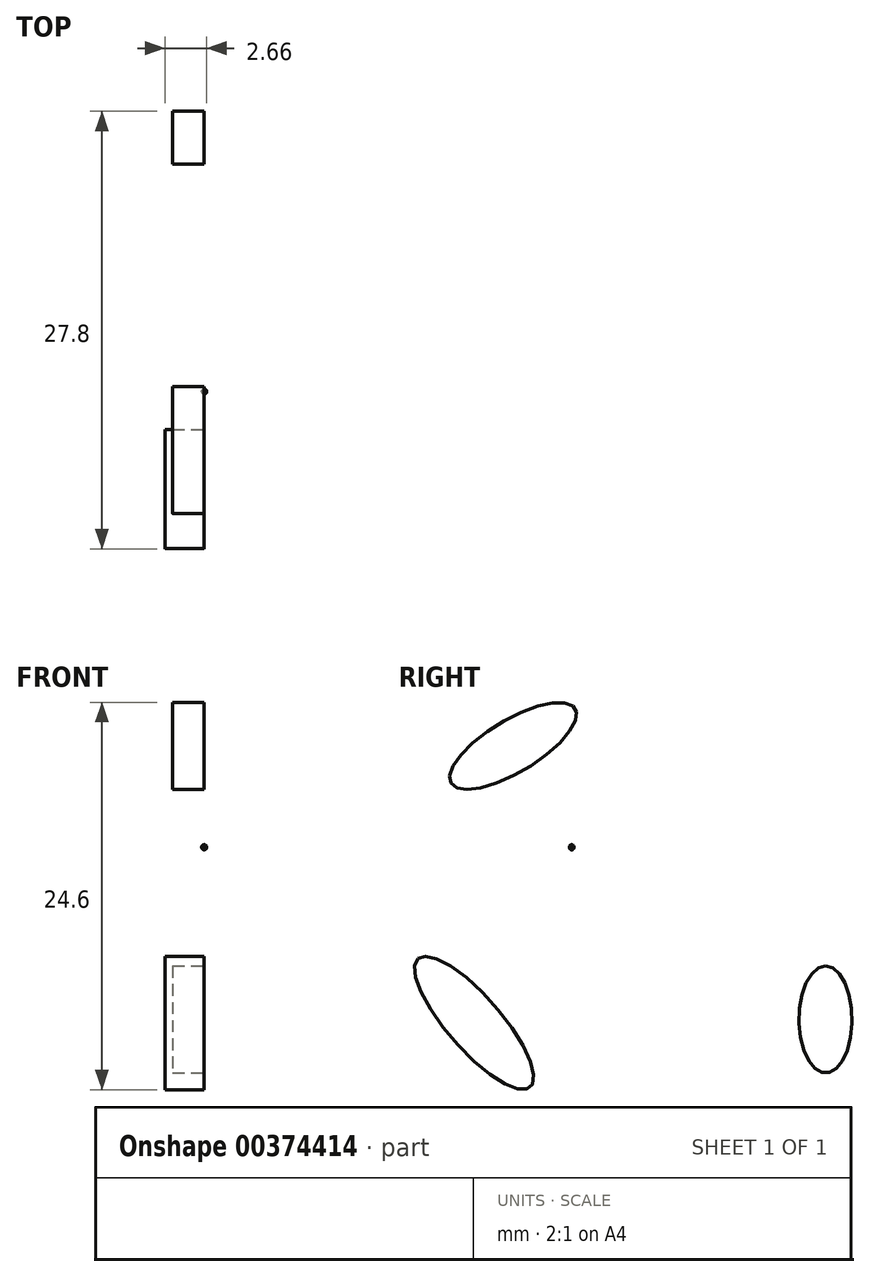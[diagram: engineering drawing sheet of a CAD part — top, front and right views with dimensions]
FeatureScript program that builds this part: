
annotation { "Feature Type Name" : "Feature", "Feature Type Description" : "" }
export const myFeature = defineFeature(function(context is Context, id is Id, definition is map)
    precondition{}
    {
        {
            var Q0;
            Q0=qCreatedBy(makeId("Front.planeOp"),FACE);
            var sketch = newSketch(context, id + "F0", { "sketchPlane" : qUnion([Q0])});
            skLineSegment(sketch, "E0", {"start": v(0, 0) * mm, "end": v(0, 20) * mm});
            skLineSegment(sketch, "E1", {"start": v(0, 0) * mm, "end": v(20.9, 0) * mm});
            skArc(sketch, "E2", {"start": v(20.9, 0) * mm, "mid": v(14.71, 14.46) * mm, "end": v(0, 20) * mm});
            skSolve(sketch);
        }
        {
            var Q0;
            Q0=makeQuery(id+"F0.imprint","IMPRINT",FACE,{"disambiguationData":[TD([[makeQuery(id+"F0.imprint","IMPRINT",EDGE,{"derivedFrom":sQuery(id+"F0.wireOp",EDGE,"E0")}),-1.0]])]});
            var Q1;
            Q1=sQuery(id+"F0.wireOp",EDGE,"E1");
            revolve(context, id + "F1", {"entities" : qUnion([Q0]), "axis" : qUnion([Q1]), "revolveType" : RevolveType.FULL});
        }
        {
            var Q0;
            Q0=qCreatedBy(makeId("Right.planeOp"),FACE);
            var sketch = newSketch(context, id + "F2", { "sketchPlane" : qUnion([Q0])});
            skLineSegment(sketch, "E3", {"start": v(0, 0) * mm, "end": v(0, 3) * mm});
            skLineSegment(sketch, "E4", {"start": v(0, 0) * mm, "end": v(-3, 0) * mm});
            skArc(sketch, "E5", {"start": v(0, 3) * mm, "mid": v(-2.14, 2.14) * mm, "end": v(-3, 0) * mm});
            skSolve(sketch);
        }
        {
            var Q0;
            Q0=qSketchRegion(id+"F2",true);
            var Q1;
            Q1=sQuery(id+"F2.wireOp",EDGE,"E4");
            revolve(context, id + "F3", {"operationType" : NewBodyOperationType.ADD, "entities" : qUnion([Q0]), "axis" : qUnion([Q1]), "revolveType" : RevolveType.FULL});
        }
        {
            var Q0;
            Q0=makeQuery(id+"F1.opRevolve","SWEPT_FACE",FACE,{"disambiguationData":[OSD([sQuery(id+"F0.wireOp",EDGE,"E0")])]});
            var sketch = newSketch(context, id + "F4", { "sketchPlane" : qUnion([Q0])});
            skLineSegment(sketch, "E6", {"start": v(0, 0) * mm, "end": v(-3, 0) * mm});
            skLineSegment(sketch, "E7", {"start": v(0, 0) * mm, "end": v(0, 3) * mm});
            skArc(sketch, "E8", {"start": v(0, 3) * mm, "mid": v(-2.1, 2.1) * mm, "end": v(-3, 0) * mm});
            skSolve(sketch);
        }
        {
            var Q0;
            Q0=makeQuery(id+"F4.imprint","IMPRINT",FACE,{"disambiguationData":[TD([[makeQuery(id+"F4.imprint","IMPRINT",EDGE,{"derivedFrom":sQuery(id+"F4.wireOp",EDGE,"E6")}),-1.0]])]});
            var Q1;
            Q1=sQuery(id+"F4.wireOp",EDGE,"E6");
            revolve(context, id + "F5", {"operationType" : NewBodyOperationType.ADD, "entities" : qUnion([Q0]), "axis" : qUnion([Q1]), "revolveType" : RevolveType.FULL});
        }
        {
            var Q0;
            Q0=makeQuery(id+"F1.opRevolve","SWEPT_FACE",FACE,{"disambiguationData":[OSD([sQuery(id+"F0.wireOp",EDGE,"E0")])]});
            var sketch = newSketch(context, id + "F6", { "sketchPlane" : qUnion([Q0])});
            skEllipse(sketch, "E9", {"center": v(9.46, -7.67) * mm, "majorRadius": 5.42 * mm, "minorRadius": 1.7 * mm, "majorAxis": v(0.66, 0.75)});
            skSolve(sketch);
        }
        {
            var Q0;
            Q0=qSketchRegion(id+"F6",true);
            extrude(context, id + "F7", {"entities" : qUnion([Q0]), "depth" : 2.5 * mm});
        }
        {
            var Q0;
            Q0=makeQuery(id+"F7.opExtrude","CAP_FACE",FACE,{"disambiguationData":[OSD([sQuery(id+"F6.wireOp",EDGE,"E9")])],"isStart":false});
            var sketch = newSketch(context, id + "F8", { "sketchPlane" : qUnion([Q0])});
            skFitSpline(sketch, "E10", {"points": [v(7.97, -11.28) * mm, v(6.8, -8.9) * mm, v(9.38, -10.19) * mm, v(8.17, -7.24) * mm, v(11, -8.49) * mm, v(9.27, -5.4) * mm, v(11.92, -6.7) * mm, v(11.05, -4) * mm, v(13.1, -5.01) * mm], "startDerivative": vector(-20.7, 30.85) * mm, "endDerivative": vector(27.66, -19.9) * mm});
            skSolve(sketch);
        }
        {
            var Q0;
            Q0=qSketchRegion(id+"F8",true);
            var Q1;
            Q1=sQuery(id+"F8.wireOp",EDGE,"E10");
            extrude(context, id + "F9", {"entities" : qUnion([Q0]), "bodyType" : ToolBodyType.SURFACE, "surfaceEntities" : qUnion([Q1]), "oppositeDirection" : true, "depth" : 2 * mm});
        }
        {
            var Q0;
            Q0=makeQuery(id+"F1.opRevolve","SWEPT_FACE",FACE,{"disambiguationData":[OSD([sQuery(id+"F0.wireOp",EDGE,"E0")])]});
            var sketch = newSketch(context, id + "F10", { "sketchPlane" : qUnion([Q0])});
            skSolve(sketch);
        }
        {
            var Q0;
            {var subQ1=sQuery(id+"F0.wireOp",EDGE,"E0");Q0=makeQuery(id+"F10.imprint","IMPRINT",FACE,{"disambiguationData":[TD([[makeQuery(id+"F10.imprint","IMPRINT",EDGE,{"derivedFrom":makeQuery(id+"F1.opRevolve","SWEPT_EDGE",EDGE,{"disambiguationData":[OSD([subQ1,sQuery(id+"F0.wireOp",EDGE,"E2")])]})}),1.0]])]});}
            var sketch = newSketch(context, id + "F11", { "sketchPlane" : qUnion([Q0])});
            skSolve(sketch);
        }
        {
            var Q0;
            {var subQ1=sQuery(id+"F0.wireOp",EDGE,"E0");Q0=makeQuery(id+"F10.imprint","IMPRINT",FACE,{"disambiguationData":[TD([[makeQuery(id+"F10.imprint","IMPRINT",EDGE,{"derivedFrom":makeQuery(id+"F1.opRevolve","SWEPT_EDGE",EDGE,{"disambiguationData":[OSD([subQ1,sQuery(id+"F0.wireOp",EDGE,"E2")])]})}),1.0]])]});}
            var sketch = newSketch(context, id + "F12", { "sketchPlane" : qUnion([Q0])});
            skEllipse(sketch, "E11", {"center": v(6.98, 9.93) * mm, "majorRadius": 4.6 * mm, "minorRadius": 1.66 * mm, "majorAxis": v(0.86, -0.51)});
            skSolve(sketch);
        }
        {
            var Q0;
            Q0=qSketchRegion(id+"F12",true);
            extrude(context, id + "F13", {"entities" : qUnion([Q0]), "depth" : 2 * mm});
        }
        {
            var Q0;
            Q0=makeQuery(id+"F13.opExtrude","CAP_FACE",FACE,{"disambiguationData":[OSD([sQuery(id+"F12.wireOp",EDGE,"E11")])],"isStart":false});
            var sketch = newSketch(context, id + "F14", { "sketchPlane" : qUnion([Q0])});
            skFitSpline(sketch, "E12", {"points": [v(4.68, 12.63) * mm, v(3.63, 10.54) * mm, v(6.2, 12.18) * mm, v(5.11, 9.18) * mm, v(7.84, 11.35) * mm, v(6.92, 8.06) * mm, v(9.45, 10.2) * mm, v(9.08, 7.26) * mm], "startDerivative": vector(-17.32, -26.87) * mm, "endDerivative": vector(-10.03, -33.63) * mm});
            skSolve(sketch);
        }
        {
            var Q0;
            Q0=qSketchRegion(id+"F14",true);
            var Q1;
            Q1=sQuery(id+"F14.wireOp",EDGE,"E12");
            extrude(context, id + "F15", {"entities" : qUnion([Q0]), "bodyType" : ToolBodyType.SURFACE, "surfaceEntities" : qUnion([Q1]), "oppositeDirection" : true, "depth" : 2 * mm});
        }
        {
            var Q0;
            {var subQ1=sQuery(id+"F0.wireOp",EDGE,"E0");Q0=makeQuery(id+"F10.imprint","IMPRINT",FACE,{"disambiguationData":[TD([[makeQuery(id+"F10.imprint","IMPRINT",EDGE,{"derivedFrom":makeQuery(id+"F1.opRevolve","SWEPT_EDGE",EDGE,{"disambiguationData":[OSD([subQ1,sQuery(id+"F0.wireOp",EDGE,"E2")])]})}),1.0]])]});}
            var sketch = newSketch(context, id + "F16", { "sketchPlane" : qUnion([Q0])});
            skFitSpline(sketch, "E13", {"points": [v(-13.4, 3.83) * mm, v(-13, 6.76) * mm, v(-11.02, 11.05) * mm, v(-7.06, 13.56) * mm, v(-3.83, 13.87) * mm, v(-2.72, 12.84) * mm, v(-4.78, 12.22) * mm, v(-7.76, 11.16) * mm, v(-9.8, 9.35) * mm, v(-10.94, 6.79) * mm, v(-11.41, 3.75) * mm, v(-10.83, 2.72) * mm, v(-9.4, 6.15) * mm, v(-7.32, 9.32) * mm, v(-3.78, 10.86) * mm, v(-3.25, 8.93) * mm, v(-5.3, 8.35) * mm, v(-7.26, 6.9) * mm, v(-8.35, 4.25) * mm, v(-7.57, 3.02) * mm, v(-6.48, 4.95) * mm, v(-5.4, 6.65) * mm, v(-2.94, 7.46) * mm, v(-2.5, 6.23) * mm, v(-4.8, 5.59) * mm, v(-6.14, 2.41) * mm], "startDerivative": vector(4.96, 65.1) * mm, "endDerivative": vector(-14.45, -88.75) * mm});
            skSolve(sketch);
        }
        {
            var Q0;
            Q0=qSketchRegion(id+"F16",true);
            var Q1;
            Q1=sQuery(id+"F16.wireOp",EDGE,"E13");
            extrude(context, id + "F17", {"entities" : qUnion([Q0]), "bodyType" : ToolBodyType.SURFACE, "surfaceEntities" : qUnion([Q1]), "depth" : 2 * mm});
        }
        {
            var Q0;
            {var subQ1=sQuery(id+"F0.wireOp",EDGE,"E0");Q0=makeQuery(id+"F10.imprint","IMPRINT",FACE,{"disambiguationData":[TD([[makeQuery(id+"F10.imprint","IMPRINT",EDGE,{"derivedFrom":makeQuery(id+"F1.opRevolve","SWEPT_EDGE",EDGE,{"disambiguationData":[OSD([subQ1,sQuery(id+"F0.wireOp",EDGE,"E2")])]})}),1.0]])]});}
            var sketch = newSketch(context, id + "F18", { "sketchPlane" : qUnion([Q0])});
            skFitSpline(sketch, "E14", {"points": [v(1.63, 7.11) * mm, v(4.78, 6.86) * mm, v(8.1, 5.2) * mm, v(9.66, 1.11) * mm, v(8.41, -3.01) * mm, v(4.67, -6.66) * mm, v(1.55, -7.21) * mm, v(1.07, -5.9) * mm, v(5.1, -4.45) * mm, v(7.63, -0.85) * mm, v(7.17, 3.33) * mm, v(4.59, 5.28) * mm, v(0, 5.94) * mm, v(0, 5.08) * mm, v(3.24, 4.42) * mm, v(5.82, 2.74) * mm, v(6.18, 0) * mm, v(5.56, -2.02) * mm, v(3.12, -3.79) * mm, v(1.15, -4.12) * mm, v(1.1, -3.42) * mm, v(3.12, -2.7) * mm, v(4.9, -0.76) * mm, v(4.7, 2.17) * mm, v(3.65, 3.54) * mm, v(1.42, 3.89) * mm, v(0, 3.94) * mm, v(0, 3.36) * mm, v(2.32, 3.19) * mm, v(3.68, 1.68) * mm, v(3.9, 0) * mm, v(3.27, -1.54) * mm, v(2.16, -2.36) * mm], "startDerivative": vector(88.94, -1.16) * mm, "endDerivative": vector(-52.62, -29.6) * mm});
            skSolve(sketch);
        }
        {
            var Q0;
            Q0=qSketchRegion(id+"F18",true);
            var Q1;
            Q1=sQuery(id+"F18.wireOp",EDGE,"E14");
            extrude(context, id + "F19", {"entities" : qUnion([Q0]), "bodyType" : ToolBodyType.SURFACE, "surfaceEntities" : qUnion([Q1]), "depth" : 1.8 * mm});
        }
        {
            var Q0;
            {var subQ1=sQuery(id+"F0.wireOp",EDGE,"E0");Q0=makeQuery(id+"F10.imprint","IMPRINT",FACE,{"disambiguationData":[TD([[makeQuery(id+"F10.imprint","IMPRINT",EDGE,{"derivedFrom":makeQuery(id+"F1.opRevolve","SWEPT_EDGE",EDGE,{"disambiguationData":[OSD([subQ1,sQuery(id+"F0.wireOp",EDGE,"E2")])]})}),1.0]])]});}
            var sketch = newSketch(context, id + "F20", { "sketchPlane" : qUnion([Q0])});
            skLineSegment(sketch, "E15", {"start": v(-7.66, -5.18) * mm, "end": v(-7.66, -3.88) * mm});
            skArc(sketch, "E16", {"start": v(-7.66, -3.88) * mm, "mid": v(-8.27, -4.53) * mm, "end": v(-7.66, -5.18) * mm});
            skSolve(sketch);
        }
        {
            var Q0;
            Q0=qSketchRegion(id+"F20",true);
            var Q1;
            Q1=sQuery(id+"F20.wireOp",EDGE,"E15");
            revolve(context, id + "F21", {"operationType" : NewBodyOperationType.ADD, "entities" : qUnion([Q0]), "axis" : qUnion([Q1]), "revolveType" : RevolveType.FULL});
        }
        {
            var Q0;
            {var subQ1=sQuery(id+"F0.wireOp",EDGE,"E0");Q0=makeQuery(id+"F10.imprint","IMPRINT",FACE,{"disambiguationData":[TD([[makeQuery(id+"F10.imprint","IMPRINT",EDGE,{"derivedFrom":makeQuery(id+"F1.opRevolve","SWEPT_EDGE",EDGE,{"disambiguationData":[OSD([subQ1,sQuery(id+"F0.wireOp",EDGE,"E2")])]})}),1.0]])]});}
            var sketch = newSketch(context, id + "F22", { "sketchPlane" : qUnion([Q0])});
            skLineSegment(sketch, "E17", {"start": v(12.74, 4.08) * mm, "end": v(12.74, 5.23) * mm});
            skArc(sketch, "E18", {"start": v(12.74, 5.23) * mm, "mid": v(12.17, 4.66) * mm, "end": v(12.74, 4.08) * mm});
            skSolve(sketch);
        }
        {
            var Q0;
            Q0=qSketchRegion(id+"F22",true);
            var Q1;
            Q1=sQuery(id+"F22.wireOp",EDGE,"E17");
            revolve(context, id + "F23", {"operationType" : NewBodyOperationType.ADD, "entities" : qUnion([Q0]), "axis" : qUnion([Q1]), "revolveType" : RevolveType.FULL});
        }
        {
            var Q0;
            {var subQ1=sQuery(id+"F0.wireOp",EDGE,"E0");Q0=makeQuery(id+"F10.imprint","IMPRINT",FACE,{"disambiguationData":[TD([[makeQuery(id+"F10.imprint","IMPRINT",EDGE,{"derivedFrom":makeQuery(id+"F1.opRevolve","SWEPT_EDGE",EDGE,{"disambiguationData":[OSD([subQ1,sQuery(id+"F0.wireOp",EDGE,"E2")])]})}),1.0]])]});}
            var sketch = newSketch(context, id + "F24", { "sketchPlane" : qUnion([Q0])});
            skLineSegment(sketch, "E19", {"start": v(-5.97, -14.13) * mm, "end": v(-5.97, -12.52) * mm});
            skArc(sketch, "E20", {"start": v(-5.97, -12.52) * mm, "mid": v(-6.78, -13.33) * mm, "end": v(-5.97, -14.13) * mm});
            skSolve(sketch);
        }
        {
            var Q0;
            Q0=qSketchRegion(id+"F24",true);
            var Q1;
            Q1=sQuery(id+"F24.wireOp",EDGE,"E19");
            revolve(context, id + "F25", {"operationType" : NewBodyOperationType.ADD, "entities" : qUnion([Q0]), "axis" : qUnion([Q1]), "revolveType" : RevolveType.FULL});
        }
        {
            var Q0;
            {var subQ1=sQuery(id+"F0.wireOp",EDGE,"E0");Q0=makeQuery(id+"F10.imprint","IMPRINT",FACE,{"disambiguationData":[TD([[makeQuery(id+"F10.imprint","IMPRINT",EDGE,{"derivedFrom":makeQuery(id+"F1.opRevolve","SWEPT_EDGE",EDGE,{"disambiguationData":[OSD([subQ1,sQuery(id+"F0.wireOp",EDGE,"E2")])]})}),1.0]])]});}
            var sketch = newSketch(context, id + "F26", { "sketchPlane" : qUnion([Q0])});
            skLineSegment(sketch, "E21", {"start": v(-3.75, 16.1) * mm, "end": v(-2.67, 17.25) * mm});
            skArc(sketch, "E22", {"start": v(-2.67, 17.25) * mm, "mid": v(-3.8, 17.24) * mm, "end": v(-3.75, 16.1) * mm});
            skSolve(sketch);
        }
        {
            var Q0;
            Q0=qSketchRegion(id+"F26",true);
            var Q1;
            Q1=sQuery(id+"F26.wireOp",EDGE,"E21");
            revolve(context, id + "F27", {"operationType" : NewBodyOperationType.ADD, "entities" : qUnion([Q0]), "axis" : qUnion([Q1]), "revolveType" : RevolveType.FULL});
        }
        {
            var Q0;
            {var subQ1=sQuery(id+"F0.wireOp",EDGE,"E0");Q0=makeQuery(id+"F10.imprint","IMPRINT",FACE,{"disambiguationData":[TD([[makeQuery(id+"F10.imprint","IMPRINT",EDGE,{"derivedFrom":makeQuery(id+"F1.opRevolve","SWEPT_EDGE",EDGE,{"disambiguationData":[OSD([subQ1,sQuery(id+"F0.wireOp",EDGE,"E2")])]})}),1.0]])]});}
            var sketch = newSketch(context, id + "F28", { "sketchPlane" : qUnion([Q0])});
            skLineSegment(sketch, "E23", {"start": v(3.12, 3.49) * mm, "end": v(3.4, 3.49) * mm});
            skArc(sketch, "E24", {"start": v(3.4, 3.49) * mm, "mid": v(3.26, 3.61) * mm, "end": v(3.12, 3.49) * mm});
            skSolve(sketch);
        }
        {
            var Q0;
            Q0=qSketchRegion(id+"F28",true);
            var Q1;
            Q1=sQuery(id+"F28.wireOp",EDGE,"E23");
            revolve(context, id + "F29", {"entities" : qUnion([Q0]), "axis" : qUnion([Q1]), "revolveType" : RevolveType.FULL});
        }
        {
            var Q0;
            {var subQ1=sQuery(id+"F0.wireOp",EDGE,"E0");Q0=makeQuery(id+"F10.imprint","IMPRINT",FACE,{"disambiguationData":[TD([[makeQuery(id+"F10.imprint","IMPRINT",EDGE,{"derivedFrom":makeQuery(id+"F1.opRevolve","SWEPT_EDGE",EDGE,{"disambiguationData":[OSD([subQ1,sQuery(id+"F0.wireOp",EDGE,"E2")])]})}),1.0]])]});}
            var sketch = newSketch(context, id + "F30", { "sketchPlane" : qUnion([Q0])});
            skLineSegment(sketch, "E25", {"start": v(1.66, 2.96) * mm, "end": v(2.07, 2.96) * mm});
            skArc(sketch, "E26", {"start": v(2.07, 2.96) * mm, "mid": v(1.86, 3.17) * mm, "end": v(1.66, 2.96) * mm});
            skSolve(sketch);
        }
        {
            var Q0;
            Q0=qSketchRegion(id+"F30",true);
            var Q1;
            Q1=sQuery(id+"F30.wireOp",EDGE,"E25");
            revolve(context, id + "F31", {"operationType" : NewBodyOperationType.ADD, "entities" : qUnion([Q0]), "axis" : qUnion([Q1]), "revolveType" : RevolveType.FULL});
        }
        {
            var Q0;
            {var subQ1=sQuery(id+"F0.wireOp",EDGE,"E0");Q0=makeQuery(id+"F10.imprint","IMPRINT",FACE,{"disambiguationData":[TD([[makeQuery(id+"F10.imprint","IMPRINT",EDGE,{"derivedFrom":makeQuery(id+"F1.opRevolve","SWEPT_EDGE",EDGE,{"disambiguationData":[OSD([subQ1,sQuery(id+"F0.wireOp",EDGE,"E2")])]})}),1.0]])]});}
            var sketch = newSketch(context, id + "F32", { "sketchPlane" : qUnion([Q0])});
            skLineSegment(sketch, "E27", {"start": v(4.55, 2) * mm, "end": v(4.73, 2) * mm});
            skArc(sketch, "E28", {"start": v(4.73, 2) * mm, "mid": v(4.64, 2.07) * mm, "end": v(4.55, 2) * mm});
            skSolve(sketch);
        }
        {
            var Q0;
            Q0=qSketchRegion(id+"F32",true);
            var Q1;
            Q1=sQuery(id+"F32.wireOp",EDGE,"E27");
            revolve(context, id + "F33", {"operationType" : NewBodyOperationType.ADD, "entities" : qUnion([Q0]), "axis" : qUnion([Q1]), "revolveType" : RevolveType.FULL});
        }
        {
            var Q0;
            {var subQ1=sQuery(id+"F0.wireOp",EDGE,"E0");Q0=makeQuery(id+"F10.imprint","IMPRINT",FACE,{"disambiguationData":[TD([[makeQuery(id+"F10.imprint","IMPRINT",EDGE,{"derivedFrom":makeQuery(id+"F1.opRevolve","SWEPT_EDGE",EDGE,{"disambiguationData":[OSD([subQ1,sQuery(id+"F0.wireOp",EDGE,"E2")])]})}),1.0]])]});}
            var sketch = newSketch(context, id + "F34", { "sketchPlane" : qUnion([Q0])});
            skLineSegment(sketch, "E29", {"start": v(4.5, -0.38) * mm, "end": v(4.7, -0.38) * mm});
            skArc(sketch, "E30", {"start": v(4.5, -0.38) * mm, "mid": v(4.6, -0.48) * mm, "end": v(4.7, -0.38) * mm});
            skSolve(sketch);
        }
        {
            var Q0;
            Q0=qSketchRegion(id+"F34",true);
            var Q1;
            Q1=sQuery(id+"F34.wireOp",EDGE,"E29");
            revolve(context, id + "F35", {"operationType" : NewBodyOperationType.ADD, "entities" : qUnion([Q0]), "axis" : qUnion([Q1]), "revolveType" : RevolveType.FULL});
        }
        {
            var Q0;
            {var subQ1=sQuery(id+"F0.wireOp",EDGE,"E0");Q0=makeQuery(id+"F10.imprint","IMPRINT",FACE,{"disambiguationData":[TD([[makeQuery(id+"F10.imprint","IMPRINT",EDGE,{"derivedFrom":makeQuery(id+"F1.opRevolve","SWEPT_EDGE",EDGE,{"disambiguationData":[OSD([subQ1,sQuery(id+"F0.wireOp",EDGE,"E2")])]})}),1.0]])]});}
            var sketch = newSketch(context, id + "F36", { "sketchPlane" : qUnion([Q0])});
            skLineSegment(sketch, "E31", {"start": v(2.2, -3.15) * mm, "end": v(2.49, -3.15) * mm});
            skArc(sketch, "E32", {"start": v(2.49, -3.15) * mm, "mid": v(2.34, -3) * mm, "end": v(2.2, -3.15) * mm});
            skSolve(sketch);
        }
        {
            var Q0;
            Q0=qSketchRegion(id+"F36",true);
            var Q1;
            Q1=sQuery(id+"F36.wireOp",EDGE,"E31");
            revolve(context, id + "F37", {"operationType" : NewBodyOperationType.ADD, "entities" : qUnion([Q0]), "axis" : qUnion([Q1]), "revolveType" : RevolveType.FULL});
        }
        {
            var Q0;
            {var subQ1=sQuery(id+"F0.wireOp",EDGE,"E0");Q0=makeQuery(id+"F10.imprint","IMPRINT",FACE,{"disambiguationData":[TD([[makeQuery(id+"F10.imprint","IMPRINT",EDGE,{"derivedFrom":makeQuery(id+"F1.opRevolve","SWEPT_EDGE",EDGE,{"disambiguationData":[OSD([subQ1,sQuery(id+"F0.wireOp",EDGE,"E2")])]})}),1.0]])]});}
            var sketch = newSketch(context, id + "F38", { "sketchPlane" : qUnion([Q0])});
            skLineSegment(sketch, "E33", {"start": v(3.6, 0.96) * mm, "end": v(3.78, 0.96) * mm});
            skArc(sketch, "E34", {"start": v(3.78, 0.96) * mm, "mid": v(3.7, 1.05) * mm, "end": v(3.6, 0.96) * mm});
            skSolve(sketch);
        }
        {
            var Q0;
            Q0=qSketchRegion(id+"F38",true);
            var Q1;
            Q1=sQuery(id+"F38.wireOp",EDGE,"E33");
            revolve(context, id + "F39", {"operationType" : NewBodyOperationType.ADD, "entities" : qUnion([Q0]), "axis" : qUnion([Q1]), "revolveType" : RevolveType.FULL});
        }
        {
            var Q0;
            {var subQ1=sQuery(id+"F0.wireOp",EDGE,"E0");Q0=makeQuery(id+"F10.imprint","IMPRINT",FACE,{"disambiguationData":[TD([[makeQuery(id+"F10.imprint","IMPRINT",EDGE,{"derivedFrom":makeQuery(id+"F1.opRevolve","SWEPT_EDGE",EDGE,{"disambiguationData":[OSD([subQ1,sQuery(id+"F0.wireOp",EDGE,"E2")])]})}),1.0]])]});}
            var sketch = newSketch(context, id + "F40", { "sketchPlane" : qUnion([Q0])});
            skLineSegment(sketch, "E35", {"start": v(0.35, 3.91) * mm, "end": v(0.56, 3.91) * mm});
            skArc(sketch, "E36", {"start": v(0.56, 3.91) * mm, "mid": v(0.46, 4.02) * mm, "end": v(0.35, 3.91) * mm});
            skSolve(sketch);
        }
        {
            var Q0;
            Q0=qSketchRegion(id+"F40",true);
            var Q1;
            Q1=sQuery(id+"F40.wireOp",EDGE,"E35");
            revolve(context, id + "F41", {"operationType" : NewBodyOperationType.ADD, "entities" : qUnion([Q0]), "axis" : qUnion([Q1]), "revolveType" : RevolveType.FULL});
        }
        {
            var Q0;
            {var subQ1=sQuery(id+"F0.wireOp",EDGE,"E0");Q0=makeQuery(id+"F10.imprint","IMPRINT",FACE,{"disambiguationData":[TD([[makeQuery(id+"F10.imprint","IMPRINT",EDGE,{"derivedFrom":makeQuery(id+"F1.opRevolve","SWEPT_EDGE",EDGE,{"disambiguationData":[OSD([subQ1,sQuery(id+"F0.wireOp",EDGE,"E2")])]})}),1.0]])]});}
            var sketch = newSketch(context, id + "F42", { "sketchPlane" : qUnion([Q0])});
            skLineSegment(sketch, "E37", {"start": v(5.24, 1) * mm, "end": v(5.43, 0.8) * mm});
            skArc(sketch, "E38", {"start": v(5.43, 0.8) * mm, "mid": v(5.44, 1) * mm, "end": v(5.24, 1) * mm});
            skSolve(sketch);
        }
        {
            var Q0;
            Q0=qSketchRegion(id+"F42",true);
            var Q1;
            Q1=sQuery(id+"F42.wireOp",EDGE,"E37");
            revolve(context, id + "F43", {"operationType" : NewBodyOperationType.ADD, "entities" : qUnion([Q0]), "axis" : qUnion([Q1]), "revolveType" : RevolveType.FULL});
        }
        {
            var Q0;
            {var subQ1=sQuery(id+"F0.wireOp",EDGE,"E0");Q0=makeQuery(id+"F11.imprint","IMPRINT",FACE,{"disambiguationData":[TD([[makeQuery(id+"F11.imprint","IMPRINT",EDGE,{"derivedFrom":makeQuery(id+"F10.imprint","IMPRINT",EDGE,{"derivedFrom":makeQuery(id+"F1.opRevolve","SWEPT_EDGE",EDGE,{"disambiguationData":[OSD([subQ1,sQuery(id+"F0.wireOp",EDGE,"E2")])]})})}),1.0]])]});}
            var sketch = newSketch(context, id + "F44", { "sketchPlane" : qUnion([Q0])});
            skLineSegment(sketch, "E39", {"start": v(4.34, -2.15) * mm, "end": v(4.53, -1.94) * mm});
            skArc(sketch, "E40", {"start": v(4.53, -1.94) * mm, "mid": v(4.33, -1.95) * mm, "end": v(4.34, -2.15) * mm});
            skSolve(sketch);
        }
        {
            var Q0;
            Q0=qSketchRegion(id+"F44",true);
            var Q1;
            Q1=sQuery(id+"F44.wireOp",EDGE,"E39");
            revolve(context, id + "F45", {"operationType" : NewBodyOperationType.ADD, "entities" : qUnion([Q0]), "axis" : qUnion([Q1]), "revolveType" : RevolveType.FULL});
        }
        {
            var Q0;
            {var subQ1=sQuery(id+"F0.wireOp",EDGE,"E0");Q0=makeQuery(id+"F11.imprint","IMPRINT",FACE,{"disambiguationData":[TD([[makeQuery(id+"F11.imprint","IMPRINT",EDGE,{"derivedFrom":makeQuery(id+"F10.imprint","IMPRINT",EDGE,{"derivedFrom":makeQuery(id+"F1.opRevolve","SWEPT_EDGE",EDGE,{"disambiguationData":[OSD([subQ1,sQuery(id+"F0.wireOp",EDGE,"E2")])]})})}),1.0]])]});}
            var sketch = newSketch(context, id + "F46", { "sketchPlane" : qUnion([Q0])});
            skLineSegment(sketch, "E41", {"start": v(3.35, -1.58) * mm, "end": v(3.52, -1.58) * mm});
            skArc(sketch, "E42", {"start": v(3.35, -1.58) * mm, "mid": v(3.43, -1.67) * mm, "end": v(3.52, -1.58) * mm});
            skSolve(sketch);
        }
        {
            var Q0;
            Q0=qSketchRegion(id+"F46",true);
            var Q1;
            Q1=sQuery(id+"F46.wireOp",EDGE,"E41");
            revolve(context, id + "F47", {"operationType" : NewBodyOperationType.ADD, "entities" : qUnion([Q0]), "axis" : qUnion([Q1]), "revolveType" : RevolveType.FULL});
        }
        {
            var Q0;
            {var subQ1=sQuery(id+"F0.wireOp",EDGE,"E0");Q0=makeQuery(id+"F11.imprint","IMPRINT",FACE,{"disambiguationData":[TD([[makeQuery(id+"F11.imprint","IMPRINT",EDGE,{"derivedFrom":makeQuery(id+"F10.imprint","IMPRINT",EDGE,{"derivedFrom":makeQuery(id+"F1.opRevolve","SWEPT_EDGE",EDGE,{"disambiguationData":[OSD([subQ1,sQuery(id+"F0.wireOp",EDGE,"E2")])]})})}),1.0]])]});}
            var sketch = newSketch(context, id + "F48", { "sketchPlane" : qUnion([Q0])});
            skEllipse(sketch, "E43", {"center": v(-12.87, -7.45) * mm, "majorRadius": 3.4 * mm, "minorRadius": 1.69 * mm, "majorAxis": v(0, 1)});
            skSolve(sketch);
        }
        {
            var Q0;
            Q0=qSketchRegion(id+"F48",true);
            extrude(context, id + "F49", {"entities" : qUnion([Q0]), "depth" : 2 * mm});
        }
        {
            var Q0;
            Q0=makeQuery(id+"F49.opExtrude","CAP_FACE",FACE,{"disambiguationData":[OSD([sQuery(id+"F48.wireOp",EDGE,"E43")])],"isStart":false});
            var sketch = newSketch(context, id + "F50", { "sketchPlane" : qUnion([Q0])});
            skFitSpline(sketch, "E44", {"points": [v(-11.66, -9.82) * mm, v(-14.04, -9.89) * mm, v(-11.29, -8.66) * mm, v(-14.53, -7.96) * mm, v(-11.19, -7.13) * mm, v(-14.5, -6.55) * mm, v(-11.4, -5.75) * mm, v(-14.12, -5.2) * mm], "startDerivative": vector(-32.3, -3.08) * mm, "endDerivative": vector(-34.6, 3.54) * mm});
            skSolve(sketch);
        }
        {
            var Q0;
            Q0=qSketchRegion(id+"F50",true);
            var Q1;
            Q1=sQuery(id+"F50.wireOp",EDGE,"E44");
            extrude(context, id + "F51", {"entities" : qUnion([Q0]), "bodyType" : ToolBodyType.SURFACE, "surfaceEntities" : qUnion([Q1]), "oppositeDirection" : true, "depth" : 2 * mm});
        }
        {
            var Q0;
            {var subQ1=sQuery(id+"F0.wireOp",EDGE,"E0");Q0=makeQuery(id+"F11.imprint","IMPRINT",FACE,{"disambiguationData":[TD([[makeQuery(id+"F11.imprint","IMPRINT",EDGE,{"derivedFrom":makeQuery(id+"F10.imprint","IMPRINT",EDGE,{"derivedFrom":makeQuery(id+"F1.opRevolve","SWEPT_EDGE",EDGE,{"disambiguationData":[OSD([subQ1,sQuery(id+"F0.wireOp",EDGE,"E2")])]})})}),1.0]])]});}
            var sketch = newSketch(context, id + "F52", { "sketchPlane" : qUnion([Q0])});
            skLineSegment(sketch, "E45", {"start": v(1.04, -10.79) * mm, "end": v(2.2, -10.79) * mm});
            skArc(sketch, "E46", {"start": v(2.2, -10.79) * mm, "mid": v(1.62, -10.22) * mm, "end": v(1.04, -10.79) * mm});
            skSolve(sketch);
        }
        {
            var Q0;
            Q0=qSketchRegion(id+"F52",true);
            var Q1;
            Q1=sQuery(id+"F52.wireOp",EDGE,"E45");
            revolve(context, id + "F53", {"operationType" : NewBodyOperationType.ADD, "entities" : qUnion([Q0]), "axis" : qUnion([Q1]), "revolveType" : RevolveType.FULL});
        }
        {
            var Q0;
            {var subQ1=sQuery(id+"F0.wireOp",EDGE,"E0");Q0=makeQuery(id+"F11.imprint","IMPRINT",FACE,{"disambiguationData":[TD([[makeQuery(id+"F11.imprint","IMPRINT",EDGE,{"derivedFrom":makeQuery(id+"F10.imprint","IMPRINT",EDGE,{"derivedFrom":makeQuery(id+"F1.opRevolve","SWEPT_EDGE",EDGE,{"disambiguationData":[OSD([subQ1,sQuery(id+"F0.wireOp",EDGE,"E2")])]})})}),1.0]])]});}
            var sketch = newSketch(context, id + "F54", { "sketchPlane" : qUnion([Q0])});
            skCircle(sketch, "E47", {"center": v(2.2, -18.68) * mm, "radius": 0.6 * mm});
            skPoint(sketch, "E47.first.point", {"position": v(2.5, -18.15) * mm});
            skPoint(sketch, "E47.second.point", {"position": v(2.25, -19.28) * mm});
            skPoint(sketch, "E47.third.point", {"position": v(1.71, -18.3) * mm});
            skSolve(sketch);
        }
        {
            var Q0;
            Q0=qSketchRegion(id+"F54",true);
            extrude(context, id + "F55", {"entities" : qUnion([Q0]), "operationType" : NewBodyOperationType.REMOVE, "depth" : 20 * mm});
        }
        {
            var Q0;
            {var subQ1=sQuery(id+"F0.wireOp",EDGE,"E0");Q0=makeQuery(id+"F11.imprint","IMPRINT",FACE,{"disambiguationData":[TD([[makeQuery(id+"F11.imprint","IMPRINT",EDGE,{"derivedFrom":makeQuery(id+"F10.imprint","IMPRINT",EDGE,{"derivedFrom":makeQuery(id+"F1.opRevolve","SWEPT_EDGE",EDGE,{"disambiguationData":[OSD([subQ1,sQuery(id+"F0.wireOp",EDGE,"E2")])]})})}),1.0]])]});}
            var sketch = newSketch(context, id + "F56", { "sketchPlane" : qUnion([Q0])});
            skCircle(sketch, "E48", {"center": v(2.91, -17.45) * mm, "radius": 1.08 * mm});
            skSolve(sketch);
        }
        {
            var Q0;
            Q0=qSketchRegion(id+"F56",true);
            extrude(context, id + "F57", {"entities" : qUnion([Q0]), "operationType" : NewBodyOperationType.REMOVE, "oppositeDirection" : true, "depth" : 25 * mm});
        }
    });
